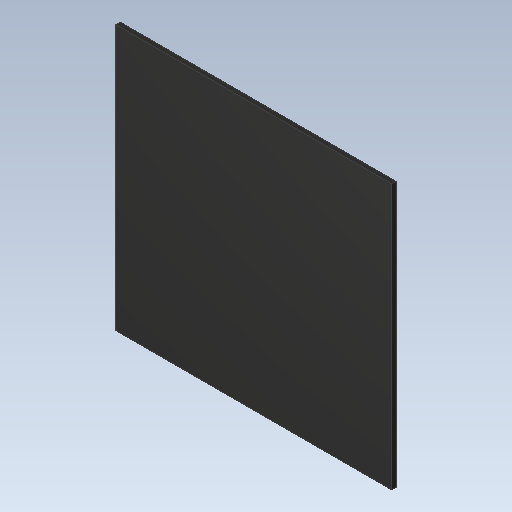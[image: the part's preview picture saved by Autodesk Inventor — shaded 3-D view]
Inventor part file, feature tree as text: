
AUTODESK INVENTOR PART (.ipt)
format: ipt  version: 2020 (Build 240168000, 168)  size: 88,064 bytes
history: imported  units: in
note: dims shown in document units (in); Inventor stores cm internally (conversion verified against a paired STEP export)
features: imported_body x1
ambient origin geometry x8: Origin, YZ Plane, XZ Plane, XY Plane, X Axis, Y Axis, Z Axis, Center Point
bodies: Solid1 (imported_parasolid), Body1 (imported_parasolid)
feature tree (1):
  imported_body  NMx_Import_Brep_tag  [imported B-rep: ~6 faces, bbox_mm=[6.35, 6.1, 0.1]]
